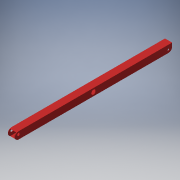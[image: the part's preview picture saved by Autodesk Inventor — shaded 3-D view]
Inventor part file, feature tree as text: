
AUTODESK INVENTOR PART (.ipt)
format: ipt  version: 2017 SP1 (Build 210196100, 196)  size: 156,672 bytes
history: native  units: in
note: dims shown in document units (in); Inventor stores cm internally (conversion verified against a paired STEP export)
features: extrude x3, sketch x3, projected_geometry x1
ambient origin geometry x8: Origin, YZ Plane, XZ Plane, XY Plane, X Axis, Y Axis, Z Axis, Center Point
bodies: Solid1 (feature_tree)
feature tree (7):
  extrude  "Extrusion1"  Depth=1.0in
  extrude  "Extrusion2"  Depth=0.0625in TaperAngle=0.0deg
  extrude  "Extrusion4"  Depth=0.5in
  sketch  "Sketch1"  dims[d0=1.0in d1=1.0in]
  sketch  "Sketch2"  dims[d2=0.0625in d3=22.0in d4=0.0in]
  sketch  "Sketch4"  dims[d5=0.625in d6=0.25in d8=1.0in d9=0.0in d13=0.5in d14=0.3866in d15=1.0in d16=0.5in d17=1.0in d18=0.0in d19=0.375in d20=0.5in d21=0.375in d22=0.25in d23=5.0in]
  projected_geometry  "Projected Loop1"
